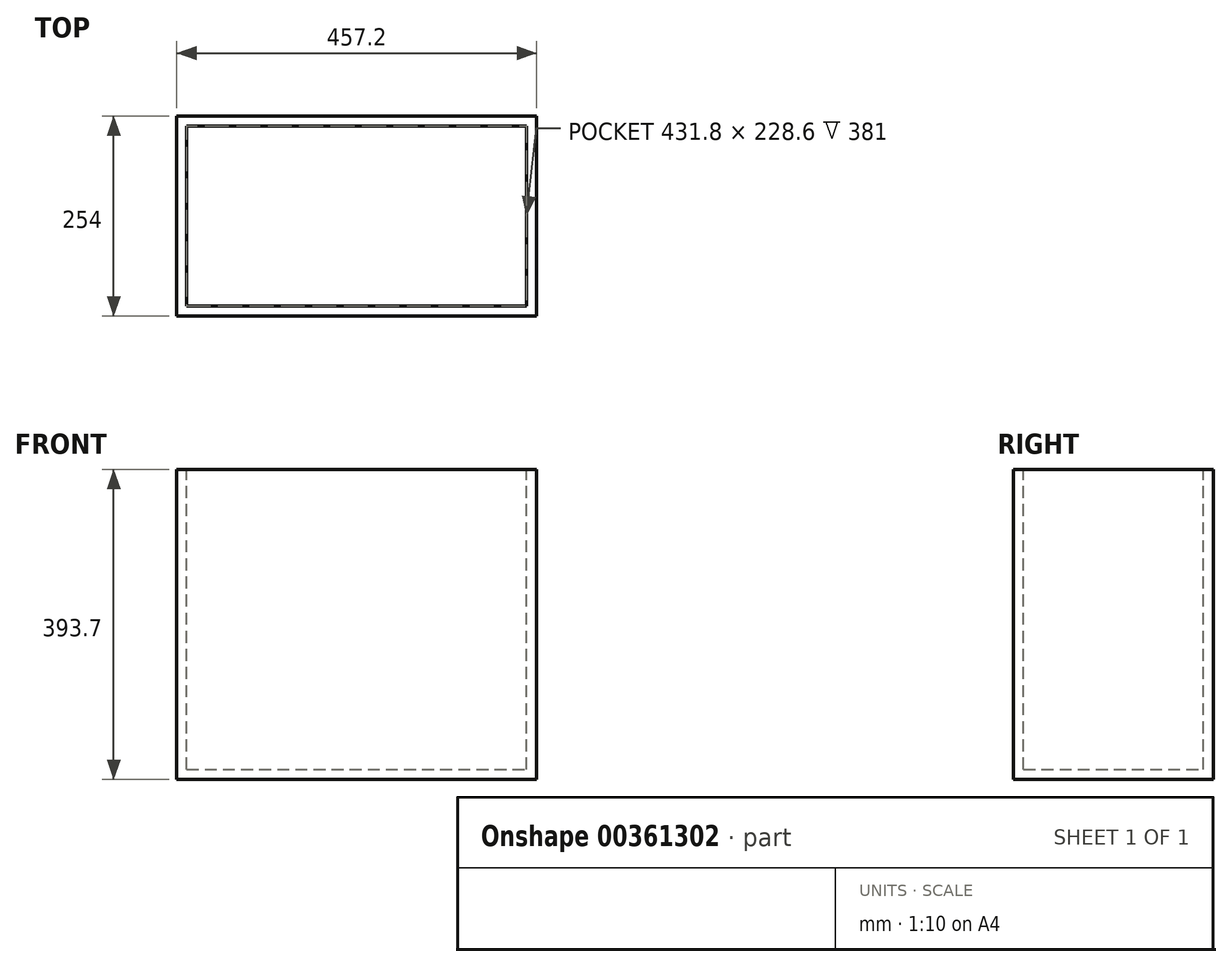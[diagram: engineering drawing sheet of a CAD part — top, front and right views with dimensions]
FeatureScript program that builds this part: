
annotation { "Feature Type Name" : "Feature", "Feature Type Description" : "" }
export const myFeature = defineFeature(function(context is Context, id is Id, definition is map)
    precondition{}
    {
        {
            var Q0;
            Q0=qCreatedBy(makeId("Front.planeOp"),FACE);
            var sketch = newSketch(context, id + "F0", { "sketchPlane" : qUnion([Q0])});
            skLineSegment(sketch, "E0.bottom", {"start": v(-215.9, -190.5) * mm, "end": v(215.9, -190.5) * mm});
            skLineSegment(sketch, "E0.top", {"start": v(-215.9, 190.5) * mm, "end": v(215.9, 190.5) * mm});
            skLineSegment(sketch, "E0.left", {"start": v(-215.9, -190.5) * mm, "end": v(-215.9, 190.5) * mm});
            skLineSegment(sketch, "E0.right", {"start": v(215.9, -190.5) * mm, "end": v(215.9, 190.5) * mm});
            skPoint(sketch, "E0.middle", {"position": v(0, 0) * mm});
            skSolve(sketch);
        }
        {
            var Q0;
            Q0=makeQuery(id+"F0.imprint","IMPRINT",FACE,{"disambiguationData":[TD([[makeQuery(id+"F0.imprint","IMPRINT",EDGE,{"derivedFrom":sQuery(id+"F0.wireOp",EDGE,"E0.bottom")}),1.0]])]});
            extrude(context, id + "F1", {"entities" : qUnion([Q0]), "depth" : 228.6 * mm});
        }
        {
            var Q0;
            Q0=makeQuery(id+"F1.opExtrude","SWEPT_FACE",FACE,{"disambiguationData":[OSD([sQuery(id+"F0.wireOp",EDGE,"E0.top")])]});
            var Q1;
            Q1=makeQuery(id+"F1.opExtrude","SWEPT_BODY",BODY,{"disambiguationData":[OSD([sQuery(id+"F0.wireOp",EDGE,"E0.bottom"),sQuery(id+"F0.wireOp",EDGE,"E0.top"),sQuery(id+"F0.wireOp",EDGE,"E0.left"),sQuery(id+"F0.wireOp",EDGE,"E0.right")])]});
            shell(context, id + "F2", {"entities" : qUnion([Q0]), "parts" : qUnion([Q1]), "thickness" : 12.7 * mm, "oppositeDirection" : true});
        }
    });
